# Revit family: Toilet-Partition_AmericanSanitary_Shower
name_source: partatom
category: Specialty Equipment
units: mm (PartAtom-declared; Revit-internal decimal feet)

## family parameters
Always vertical = Yes
Classification Number = 23.25.40.14.14.11
Cut with Voids When Loaded = No
Enable Cutting in Views = No
Host = Wall
Maintain Annotation Orientation = No
Part Type = Normal
Room Calculation Point = No
Round Connector Dimension = Use Diameter
Shared = No

## types (1)
- As Specified in 10 21 00
    Assembly Code = C1010400
    Brackets_Vertical = 2
    Construction Details = http://www.arcat.com
    Default Elevation = 0' - 0"
    Description = As Specified in 10 21 00
    Distance from Floor to Panel = 1' - 0"
    Door Height = 4' - 10"
    Door Thickness = 0' - 1"
    Door Width = 2' - 0"
    Expected Lifespan (Years) = 0
    Front Panel Width_Hinge Side = 0' - 6"
    Front Panel Width_Strike Side = 0' - 6"
    Green Building-LEED = http://www.arcat.com
    Headrail Material = Aluminum - Extruded - Satin Anodized Finish
    Installation-Fabrication = http://www.arcat.com
    Keynote = 10 21 00
    Maintenance Schedule (Months) = 0
    Manufacturer = American Sanitary Partition Corp.
    Manufacturer Fax = 407-656-8189
    Manufacturer Website = http://www.am-sanitary-partition.com
    Model = As Specified in 10 21 00
    Panel Thickness = 0' - 1"
    Pilaster Height = 6' - 10"
    Product Data = http://www.arcat.com
    Product Properties = http://www.arcat.com
    Reveal Clearance = 0' - 0 1/2"
    Revision = R1_10/2009
    Sales Information = http://www.am-sanitary-partition.com
    Send Message = http://admin.arcat.com
    Shower Seat = Plastic Laminate - White
    SpecWizard = http://www.arcat.com
    Specification = http://www.arcat.com
    Stall Width = 3' - 0"
    Stile Thickness = 0' - 1 1/4"
    Type Comments = Toilet Partition
    URL = http://www.am-sanitary-partition.com
    Warranty Duration (Years) = 0
    capoffset = 0' - 0 1/4"
    topoffset = 0' - 0 1/4"

## geometry (parser evidence)
native form markers: Blend x44, Sweep x2
no freeform markers — native parametric forms only
